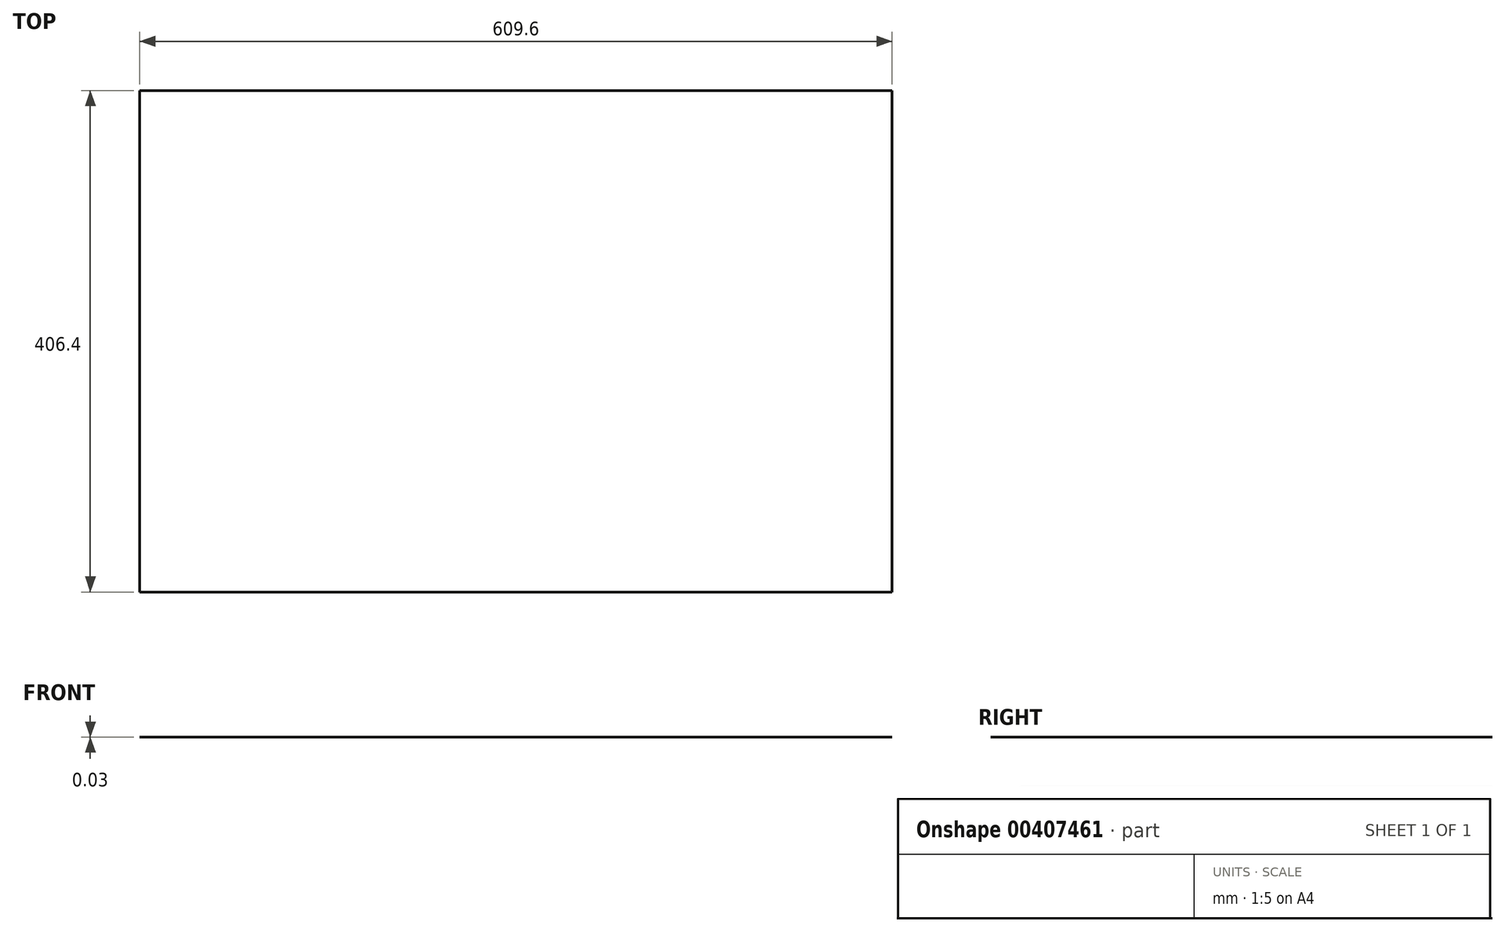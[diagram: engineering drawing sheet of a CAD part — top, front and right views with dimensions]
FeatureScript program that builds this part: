
annotation { "Feature Type Name" : "Feature", "Feature Type Description" : "" }
export const myFeature = defineFeature(function(context is Context, id is Id, definition is map)
    precondition{}
    {
        {
            var Q0;
            Q0=qCreatedBy(makeId("Top.planeOp"),FACE);
            var sketch = newSketch(context, id + "F0", { "sketchPlane" : qUnion([Q0])});
            skLineSegment(sketch, "E0.bottom", {"start": v(0, 0) * mm, "end": v(609.6, 0) * mm});
            skLineSegment(sketch, "E0.top", {"start": v(0, 406.4) * mm, "end": v(609.6, 406.4) * mm});
            skLineSegment(sketch, "E0.left", {"start": v(0, 0) * mm, "end": v(0, 406.4) * mm});
            skLineSegment(sketch, "E0.right", {"start": v(609.6, 0) * mm, "end": v(609.6, 406.4) * mm});
            skSolve(sketch);
        }
        {
            var Q0;
            Q0 = qSketchRegion(id + "F0", true);
            extrude(context, id + "F1", {"entities" : qUnion([Q0]), "depth" : 0.03 * mm});
        }
    });
